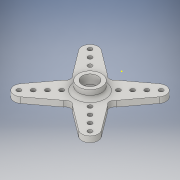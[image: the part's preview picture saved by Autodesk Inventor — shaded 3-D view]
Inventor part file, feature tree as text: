
AUTODESK INVENTOR PART (.ipt)
format: ipt  version: 2016 (Build 200138000, 138)  size: 222,208 bytes
history: native  units: in
note: dims shown in document units (in); Inventor stores cm internally (conversion verified against a paired STEP export)
features: sketch x4, extrude x2, pattern_circular x1, fillet x1
ambient origin geometry x8: Origin, YZ Plane, XZ Plane, XY Plane, X Axis, Y Axis, Z Axis, Center Point
bodies: Solid1 (feature_tree)
feature tree (8):
  pattern_circular  "CirPattern1"
  fillet  "Fillet1"  Radius=0.05in
  sketch  "Sketch1"  dims[d1=0.125in d2=0.0in d3=0.05in d4=0.0in]
  extrude  "Extrusion1"  Depth=0.05in TaperAngle=0.0deg
  sketch  "Sketch3"
  extrude  "Extrusion2"  [1 undecoded]
  sketch  "Sketch2"
  sketch  "Sketch4"
note: 1 required parameter value undecoded (feature->parameter linkage not recoverable at this tier; creation-order binding heuristic only, values carry confidence <= 0.55)
